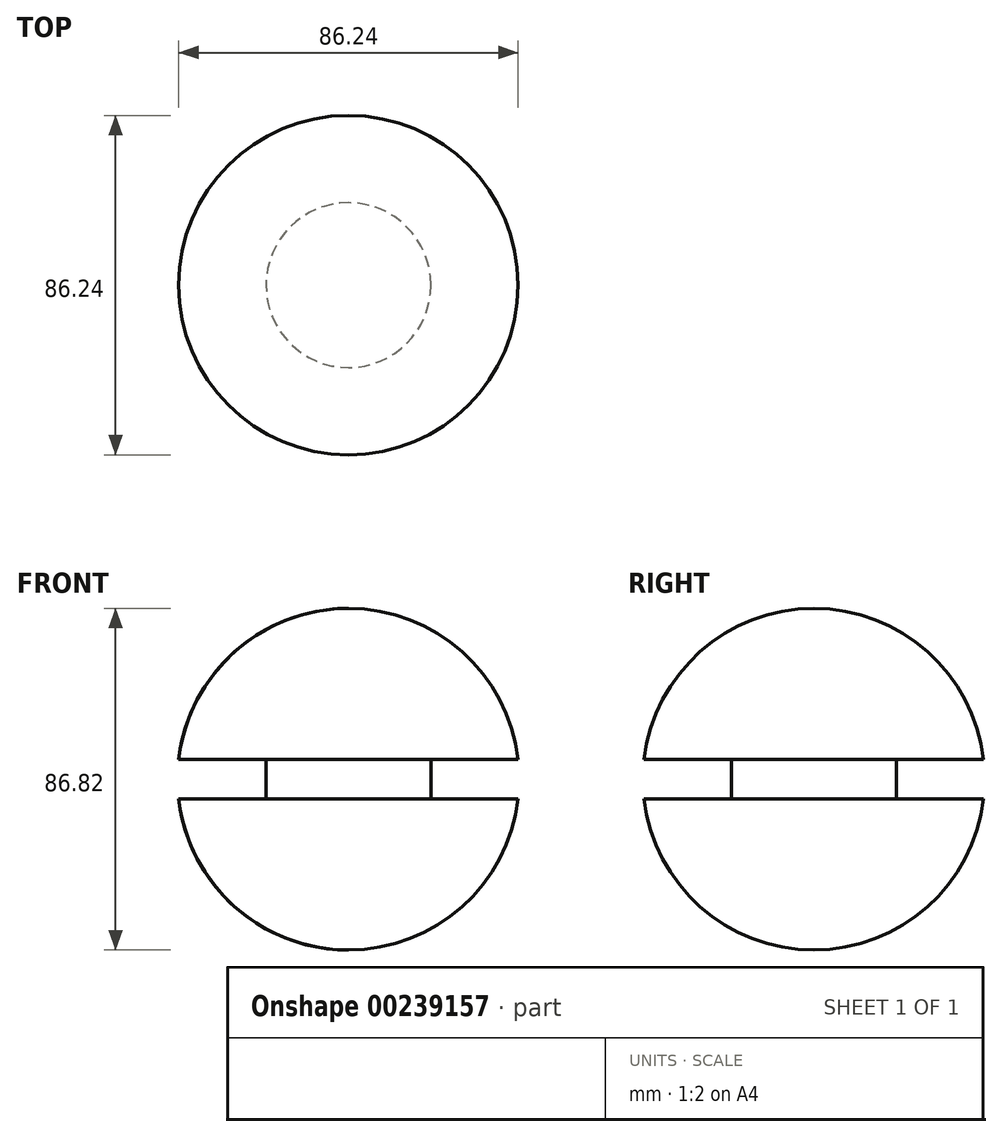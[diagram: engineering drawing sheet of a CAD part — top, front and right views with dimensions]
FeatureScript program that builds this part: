
annotation { "Feature Type Name" : "Feature", "Feature Type Description" : "" }
export const myFeature = defineFeature(function(context is Context, id is Id, definition is map)
    precondition{}
    {
        {
            var Q0;
            Q0=qCreatedBy(makeId("Front.planeOp"),FACE);
            var sketch = newSketch(context, id + "F0", { "sketchPlane" : qUnion([Q0])});
            skArc(sketch, "E0", {"start": v(0, -43.4) * mm, "mid": v(43.4, 0) * mm, "end": v(0, 43.4) * mm});
            skLineSegment(sketch, "E1", {"start": v(0, 43.4) * mm, "end": v(0, -43.4) * mm});
            skSolve(sketch);
        }
        {
            var Q0;
            Q0=makeQuery(id+"F0.imprint","IMPRINT",FACE,{"disambiguationData":[TD([[makeQuery(id+"F0.imprint","IMPRINT",EDGE,{"derivedFrom":sQuery(id+"F0.wireOp",EDGE,"E0")}),1.0]])]});
            var Q1;
            Q1=sQuery(id+"F0.wireOp",EDGE,"E1");
            revolve(context, id + "F1", {"entities" : qUnion([Q0]), "axis" : qUnion([Q1]), "revolveType" : RevolveType.FULL});
        }
        {
            var Q0;
            Q0=qCreatedBy(makeId("Front.planeOp"),FACE);
            var sketch = newSketch(context, id + "F2", { "sketchPlane" : qUnion([Q0])});
            skLineSegment(sketch, "E2.bottom", {"start": v(0, 44.45) * mm, "end": v(0, 44.45) * mm});
            skLineSegment(sketch, "E2.top", {"start": v(0, -41.72) * mm, "end": v(0, -41.72) * mm});
            skLineSegment(sketch, "E2.left", {"start": v(0, 44.45) * mm, "end": v(0, -41.72) * mm, "construction": true});
            skLineSegment(sketch, "E2.right", {"start": v(0, 44.45) * mm, "end": v(0, -41.72) * mm, "construction": true});
            skLineSegment(sketch, "E3.bottom", {"start": v(53.7, 5) * mm, "end": v(20.93, 5) * mm});
            skLineSegment(sketch, "E3.top", {"start": v(53.7, -5) * mm, "end": v(20.93, -5) * mm});
            skLineSegment(sketch, "E3.left", {"start": v(53.7, 5) * mm, "end": v(53.7, -5) * mm});
            skLineSegment(sketch, "E3.right", {"start": v(20.93, 5) * mm, "end": v(20.93, -5) * mm});
            skPoint(sketch, "E3.middle", {"position": v(37.32, 0) * mm});
            skSolve(sketch);
        }
        {
            var Q0;
            Q0=makeQuery(id+"F2.imprint","IMPRINT",FACE,{"disambiguationData":[TD([[makeQuery(id+"F2.imprint","IMPRINT",EDGE,{"derivedFrom":sQuery(id+"F2.wireOp",EDGE,"E3.bottom")}),1.0]])]});
            var Q1;
            Q1=sQuery(id+"F2.wireOp",EDGE,"E2.right");
            revolve(context, id + "F3", {"operationType" : NewBodyOperationType.REMOVE, "entities" : qUnion([Q0]), "axis" : qUnion([Q1]), "revolveType" : RevolveType.FULL, "oppositeDirection" : true});
        }
    });
